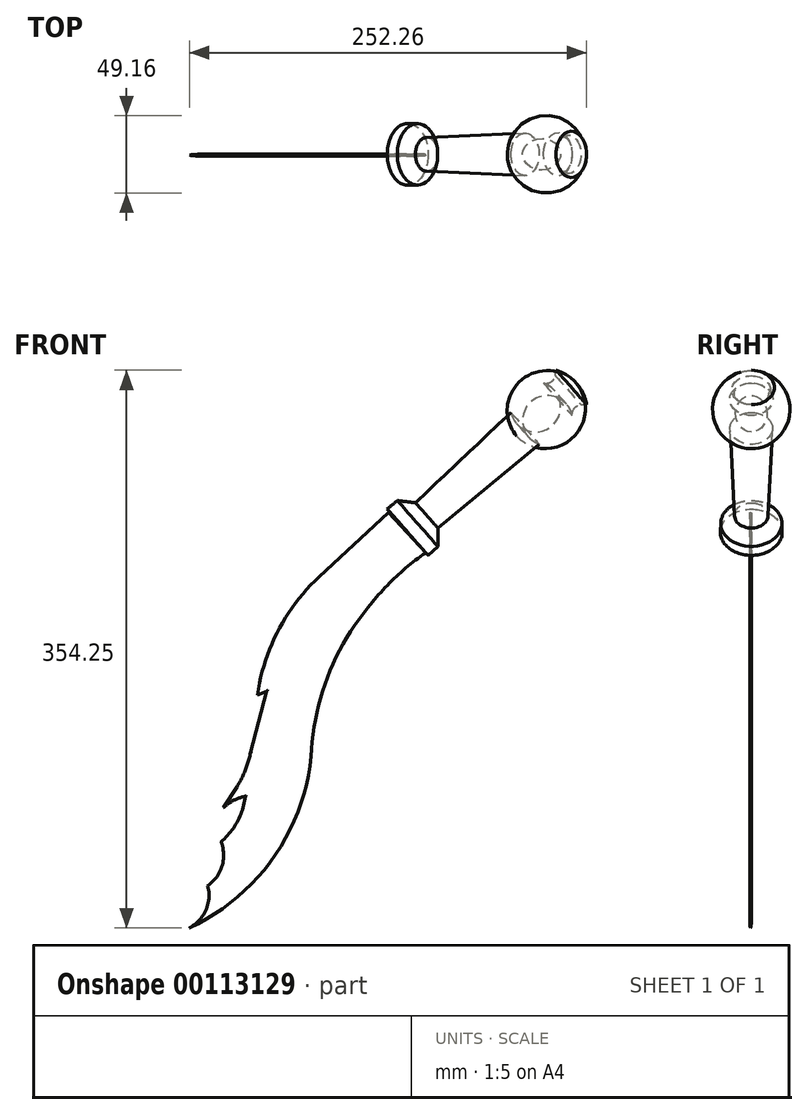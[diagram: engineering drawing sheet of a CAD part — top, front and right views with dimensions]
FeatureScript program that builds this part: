
annotation { "Feature Type Name" : "Feature", "Feature Type Description" : "" }
export const myFeature = defineFeature(function(context is Context, id is Id, definition is map)
    precondition{}
    {
        {
            var Q0;
            Q0=qCreatedBy(makeId("Front.planeOp"),FACE);
            var sketch = newSketch(context, id + "F0", { "sketchPlane" : qUnion([Q0])});
            skLineSegment(sketch, "E0", {"start": v(-106.68, 374.44) * mm, "end": v(-41.68, 374.44) * mm});
            skArc(sketch, "E1", {"start": v(-258.86, 13.26) * mm, "mid": v(-248.41, 24.62) * mm, "end": v(-247.22, 40) * mm});
            skArc(sketch, "E2", {"start": v(-247.22, 40) * mm, "mid": v(-238.16, 52.5) * mm, "end": v(-238.77, 67.92) * mm});
            skArc(sketch, "E3", {"start": v(-238.77, 67.92) * mm, "mid": v(-228.37, 80.95) * mm, "end": v(-223.34, 96.83) * mm});
            skArc(sketch, "E4", {"start": v(-223.34, 96.83) * mm, "mid": v(-230.76, 94.24) * mm, "end": v(-237.17, 89.7) * mm});
            skLineSegment(sketch, "E5", {"start": v(-237.17, 89.7) * mm, "end": v(-228.77, 102.87) * mm});
            skArc(sketch, "E6", {"start": v(-228.77, 102.87) * mm, "mid": v(-223.4, 113.34) * mm, "end": v(-220.07, 124.62) * mm});
            skLineSegment(sketch, "E7", {"start": v(-220.07, 124.62) * mm, "end": v(-209.94, 163.47) * mm});
            skLineSegment(sketch, "E8", {"start": v(-209.94, 163.47) * mm, "end": v(-215.62, 161.35) * mm});
            skArc(sketch, "E9", {"start": v(-176.48, 236.2) * mm, "mid": v(-202.5, 202.15) * mm, "end": v(-215.62, 161.35) * mm});
            skLineSegment(sketch, "E10", {"start": v(-176.48, 236.2) * mm, "end": v(-132.43, 277.05) * mm});
            skLineSegment(sketch, "E11", {"start": v(-132.43, 277.05) * mm, "end": v(-133.95, 278.68) * mm});
            skLineSegment(sketch, "E12", {"start": v(-133.95, 278.68) * mm, "end": v(-127.83, 284.36) * mm});
            skLineSegment(sketch, "E13", {"start": v(-127.83, 284.36) * mm, "end": v(-116.18, 284.36) * mm});
            skLineSegment(sketch, "E14", {"start": v(-116.18, 284.36) * mm, "end": v(-54.77, 338.67) * mm});
            skArc(sketch, "E15", {"start": v(-33.75, 356.95) * mm, "mid": v(-49.62, 353.97) * mm, "end": v(-54.77, 338.67) * mm});
            skLineSegment(sketch, "E16", {"start": v(-26.5, 363.16) * mm, "end": v(-26.5, 366.7) * mm});
            skLineSegment(sketch, "E17", {"start": v(-101.14, 267.23) * mm, "end": v(-36.78, 320.4) * mm});
            skArc(sketch, "E18", {"start": v(-36.78, 320.4) * mm, "mid": v(-20.9, 323.39) * mm, "end": v(-15.76, 338.69) * mm});
            skArc(sketch, "E19", {"start": v(-10.15, 345.55) * mm, "mid": v(-14.37, 343.28) * mm, "end": v(-15.76, 338.69) * mm});
            skLineSegment(sketch, "E20", {"start": v(-10.15, 345.55) * mm, "end": v(-6.6, 345.55) * mm});
            skArc(sketch, "E21", {"start": v(-6.6, 345.55) * mm, "mid": v(-13.22, 359.26) * mm, "end": v(-26.5, 366.7) * mm});
            skLineSegment(sketch, "E22", {"start": v(-101.14, 267.23) * mm, "end": v(-101.14, 255.58) * mm});
            skLineSegment(sketch, "E23", {"start": v(-101.14, 255.58) * mm, "end": v(-107.26, 249.9) * mm});
            skLineSegment(sketch, "E24", {"start": v(-107.26, 249.9) * mm, "end": v(-108.77, 251.54) * mm});
            skArc(sketch, "E25", {"start": v(-108.77, 251.54) * mm, "mid": v(-126.78, 237.13) * mm, "end": v(-142.5, 220.26) * mm});
            skArc(sketch, "E26", {"start": v(-142.5, 220.26) * mm, "mid": v(-170.37, 174.51) * mm, "end": v(-181.62, 122.14) * mm});
            skArc(sketch, "E27", {"start": v(-258.86, 13.26) * mm, "mid": v(-205.8, 57.45) * mm, "end": v(-181.62, 122.14) * mm});
            skArc(sketch, "E28", {"start": v(-33.75, 356.95) * mm, "mid": v(-28.7, 358.39) * mm, "end": v(-26.5, 363.16) * mm});
            skLineSegment(sketch, "E29", {"start": v(-132.43, 277.05) * mm, "end": v(-108.77, 251.54) * mm});
            skLineSegment(sketch, "E30", {"start": v(-120.6, 264.3) * mm, "end": v(-13.22, 359.26) * mm});
            skSolve(sketch);
        }
        {
            var Q0;
            Q0=makeQuery(id+"F0.imprint","IMPRINT",FACE,{"disambiguationData":[TD([[makeQuery(id+"F0.imprint","IMPRINT",EDGE,{"derivedFrom":sQuery(id+"F0.wireOp",EDGE,"E17")}),1.0]])]});
            var Q1;
            Q1=sQuery(id+"F0.wireOp",EDGE,"E30");
            revolve(context, id + "F1", {"entities" : qUnion([Q0]), "axis" : qUnion([Q1]), "revolveType" : RevolveType.FULL});
        }
        {
            var Q0;
            Q0=makeQuery(id+"F0.imprint","IMPRINT",FACE,{"disambiguationData":[TD([[makeQuery(id+"F0.imprint","IMPRINT",EDGE,{"derivedFrom":sQuery(id+"F0.wireOp",EDGE,"E1")}),-1.0]])]});
            extrude(context, id + "F2", {"entities" : qUnion([Q0]), "depth" : 1 * mm});
        }
        {
            var Q0;
            Q0=makeQuery(id+"F2.opExtrude","CAP_FACE",FACE,{"disambiguationData":[OSD([sQuery(id+"F0.wireOp",EDGE,"E1"),sQuery(id+"F0.wireOp",EDGE,"E2"),sQuery(id+"F0.wireOp",EDGE,"E3"),sQuery(id+"F0.wireOp",EDGE,"E4"),sQuery(id+"F0.wireOp",EDGE,"E5"),sQuery(id+"F0.wireOp",EDGE,"E6"),sQuery(id+"F0.wireOp",EDGE,"E7"),sQuery(id+"F0.wireOp",EDGE,"E8"),sQuery(id+"F0.wireOp",EDGE,"E9"),sQuery(id+"F0.wireOp",EDGE,"E10"),sQuery(id+"F0.wireOp",EDGE,"E25"),sQuery(id+"F0.wireOp",EDGE,"E26"),sQuery(id+"F0.wireOp",EDGE,"E27"),sQuery(id+"F0.wireOp",EDGE,"E29")])],"isStart":true});
            var Q1;
            Q1=makeQuery(id+"F2.opExtrude","CAP_FACE",FACE,{"disambiguationData":[OSD([sQuery(id+"F0.wireOp",EDGE,"E1"),sQuery(id+"F0.wireOp",EDGE,"E2"),sQuery(id+"F0.wireOp",EDGE,"E3"),sQuery(id+"F0.wireOp",EDGE,"E4"),sQuery(id+"F0.wireOp",EDGE,"E5"),sQuery(id+"F0.wireOp",EDGE,"E6"),sQuery(id+"F0.wireOp",EDGE,"E7"),sQuery(id+"F0.wireOp",EDGE,"E8"),sQuery(id+"F0.wireOp",EDGE,"E9"),sQuery(id+"F0.wireOp",EDGE,"E10"),sQuery(id+"F0.wireOp",EDGE,"E25"),sQuery(id+"F0.wireOp",EDGE,"E26"),sQuery(id+"F0.wireOp",EDGE,"E27"),sQuery(id+"F0.wireOp",EDGE,"E29")])],"isStart":false});
            fillet(context, id + "F3", {"entities" : qUnion([Q0, Q1]), "radius" : 0.5 * mm, "tangentPropagation" : true, "allowEdgeOverflow" : false});
        }
    });
